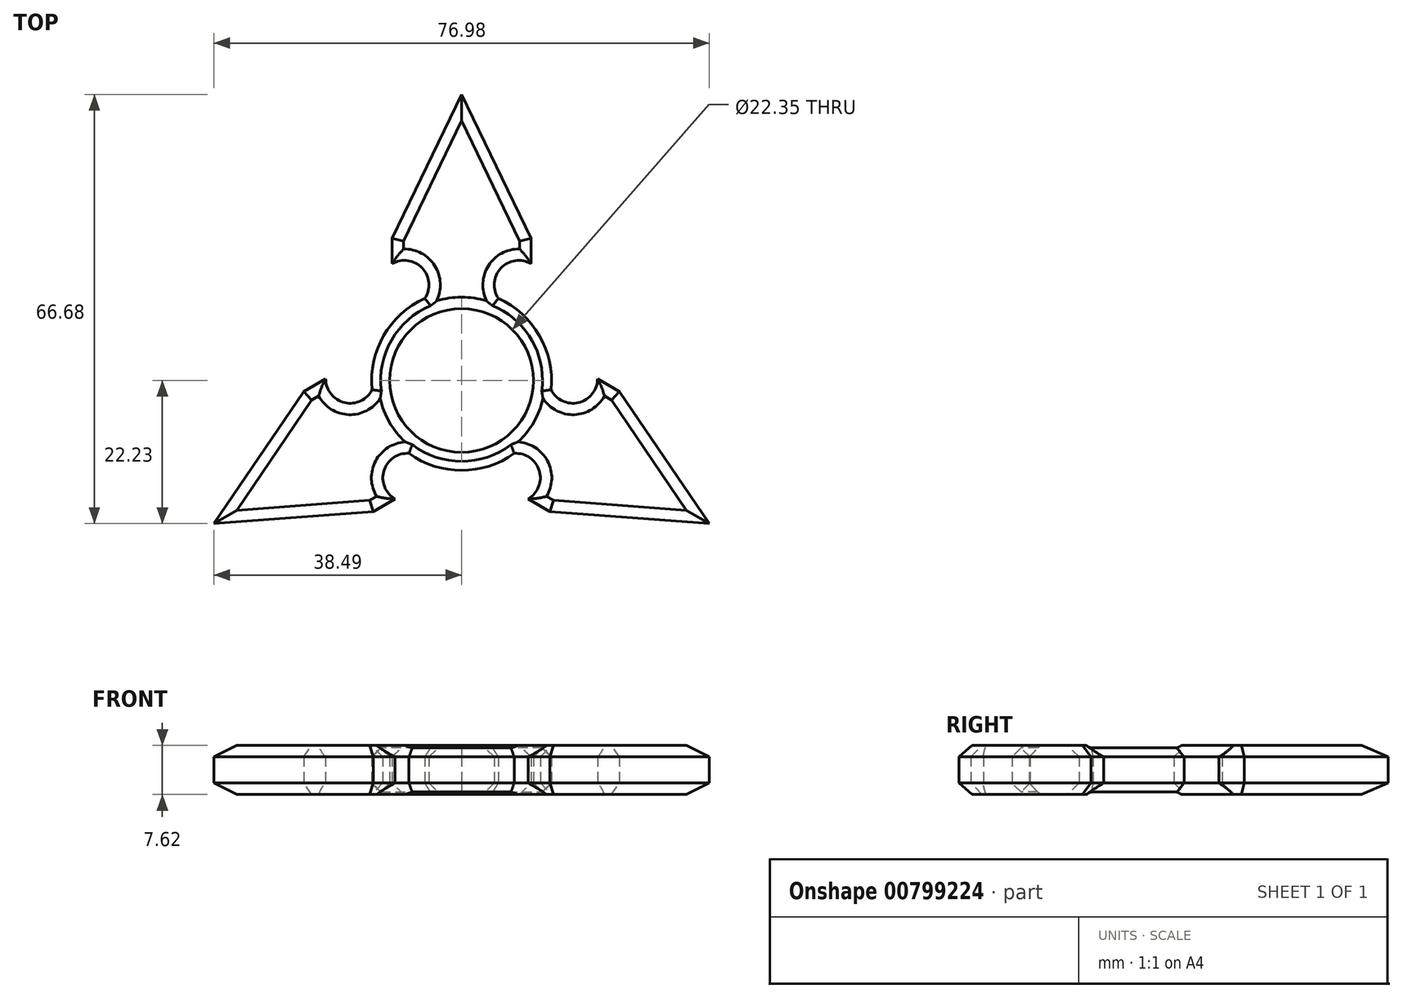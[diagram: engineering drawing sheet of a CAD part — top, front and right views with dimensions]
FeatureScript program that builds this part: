
annotation { "Feature Type Name" : "Feature", "Feature Type Description" : "" }
export const myFeature = defineFeature(function(context is Context, id is Id, definition is map)
    precondition{}
    {
        {
            var Q0;
            Q0=qCreatedBy(makeId("Top.planeOp"),FACE);
            var sketch = newSketch(context, id + "F0", { "sketchPlane" : qUnion([Q0])});
            skCircle(sketch, "E0", {"center": v(0, 0) * mm, "radius": 11.18 * mm});
            skCircle(sketch, "E1", {"center": v(0, 0) * mm, "radius": 13.97 * mm});
            skArc(sketch, "E2", {"start": v(-5.72, 12.75) * mm, "mid": v(-6.1, 17.46) * mm, "end": v(-10.78, 18.16) * mm});
            skLineSegment(sketch, "E3", {"start": v(-10.78, 18.16) * mm, "end": v(-10.78, 22.09) * mm});
            skLineSegment(sketch, "E4", {"start": v(-10.78, 22.09) * mm, "end": v(0, 44.45) * mm});
            skLineSegment(sketch, "E5.MirrorCS", {"start": v(10.78, 18.16) * mm, "end": v(10.78, 22.09) * mm});
            skArc(sketch, "E6.MirrorCS", {"start": v(5.72, 12.75) * mm, "mid": v(6.1, 17.46) * mm, "end": v(10.78, 18.16) * mm});
            skLineSegment(sketch, "E7.MirrorCS", {"start": v(10.78, 22.09) * mm, "end": v(0, 44.45) * mm});
            skLineSegment(sketch, "E8.1.0", {"start": v(-13.74, -20.38) * mm, "end": v(-38.5, -22.22) * mm});
            skLineSegment(sketch, "E8.1.1", {"start": v(-24.52, -1.7) * mm, "end": v(-38.5, -22.22) * mm});
            skArc(sketch, "E8.1.2", {"start": v(-13.9, -1.42) * mm, "mid": v(-18.17, -3.44) * mm, "end": v(-21.12, 0.25) * mm});
            skArc(sketch, "E8.1.3", {"start": v(-8.18, -11.32) * mm, "mid": v(-12.06, -14.02) * mm, "end": v(-10.34, -18.42) * mm});
            skLineSegment(sketch, "E8.1.4", {"start": v(-10.34, -18.42) * mm, "end": v(-13.74, -20.38) * mm});
            skLineSegment(sketch, "E8.1.5", {"start": v(-21.12, 0.25) * mm, "end": v(-24.52, -1.7) * mm});
            skLineSegment(sketch, "E8.2.0", {"start": v(24.52, -1.7) * mm, "end": v(38.5, -22.23) * mm});
            skLineSegment(sketch, "E8.2.1", {"start": v(13.74, -20.38) * mm, "end": v(38.5, -22.22) * mm});
            skArc(sketch, "E8.2.2", {"start": v(8.18, -11.32) * mm, "mid": v(12.06, -14.02) * mm, "end": v(10.34, -18.42) * mm});
            skArc(sketch, "E8.2.3", {"start": v(13.9, -1.42) * mm, "mid": v(18.17, -3.44) * mm, "end": v(21.12, 0.25) * mm});
            skLineSegment(sketch, "E8.2.4", {"start": v(21.12, 0.25) * mm, "end": v(24.52, -1.7) * mm});
            skLineSegment(sketch, "E8.2.5", {"start": v(10.34, -18.42) * mm, "end": v(13.74, -20.38) * mm});
            skSolve(sketch);
        }
        {
            var Q0;
            {var subQ0=sQuery(id+"F0.wireOp",EDGE,"E2");Q0=makeQuery(id+"F0.imprint","IMPRINT",FACE,{"disambiguationData":[TD([[makeQuery(id+"F0.imprint","IMPRINT",EDGE,{"derivedFrom":subQ0}),-1.0]])]});}
            var Q1;
            Q1=makeQuery(id+"F0.imprint","IMPRINT",FACE,{"disambiguationData":[TD([[makeQuery(id+"F0.imprint","IMPRINT",EDGE,{"derivedFrom":sQuery(id+"F0.wireOp",EDGE,"E0")}),-1.0]])]});
            var Q2;
            Q2=makeQuery(id+"F0.imprint","IMPRINT",FACE,{"disambiguationData":[TD([[makeQuery(id+"F0.imprint","IMPRINT",EDGE,{"derivedFrom":sQuery(id+"F0.wireOp",EDGE,"E8.2.0")}),-1.0]])]});
            var Q3;
            Q3=makeQuery(id+"F0.imprint","IMPRINT",FACE,{"disambiguationData":[TD([[makeQuery(id+"F0.imprint","IMPRINT",EDGE,{"derivedFrom":sQuery(id+"F0.wireOp",EDGE,"E8.1.0")}),-1.0]])]});
            extrude(context, id + "F1", {"entities" : qUnion([Q0, Q1, Q2, Q3]), "depth" : 7.62 * mm, "offsetDistance" : 25.4 * mm});
        }
        {
            var Q0;
            Q0=makeQuery(id+"F1.opExtrude","CAP_FACE",FACE,{"disambiguationData":[OSD([sQuery(id+"F0.wireOp",EDGE,"E0"),sQuery(id+"F0.wireOp",EDGE,"E1"),sQuery(id+"F0.wireOp",EDGE,"E2"),sQuery(id+"F0.wireOp",EDGE,"E3"),sQuery(id+"F0.wireOp",EDGE,"E4"),sQuery(id+"F0.wireOp",EDGE,"E5.MirrorCS"),sQuery(id+"F0.wireOp",EDGE,"E6.MirrorCS"),sQuery(id+"F0.wireOp",EDGE,"E7.MirrorCS"),sQuery(id+"F0.wireOp",EDGE,"E8.1.0"),sQuery(id+"F0.wireOp",EDGE,"E8.1.1"),sQuery(id+"F0.wireOp",EDGE,"E8.1.2"),sQuery(id+"F0.wireOp",EDGE,"E8.1.3"),sQuery(id+"F0.wireOp",EDGE,"E8.1.4"),sQuery(id+"F0.wireOp",EDGE,"E8.1.5"),sQuery(id+"F0.wireOp",EDGE,"E8.2.0"),sQuery(id+"F0.wireOp",EDGE,"E8.2.1"),sQuery(id+"F0.wireOp",EDGE,"E8.2.2"),sQuery(id+"F0.wireOp",EDGE,"E8.2.3"),sQuery(id+"F0.wireOp",EDGE,"E8.2.4"),sQuery(id+"F0.wireOp",EDGE,"E8.2.5")])],"isStart":false});
            var Q1;
            Q1=makeQuery(id+"F1.opExtrude","CAP_FACE",FACE,{"disambiguationData":[OSD([sQuery(id+"F0.wireOp",EDGE,"E0"),sQuery(id+"F0.wireOp",EDGE,"E1"),sQuery(id+"F0.wireOp",EDGE,"E2"),sQuery(id+"F0.wireOp",EDGE,"E3"),sQuery(id+"F0.wireOp",EDGE,"E4"),sQuery(id+"F0.wireOp",EDGE,"E5.MirrorCS"),sQuery(id+"F0.wireOp",EDGE,"E6.MirrorCS"),sQuery(id+"F0.wireOp",EDGE,"E7.MirrorCS"),sQuery(id+"F0.wireOp",EDGE,"E8.1.0"),sQuery(id+"F0.wireOp",EDGE,"E8.1.1"),sQuery(id+"F0.wireOp",EDGE,"E8.1.2"),sQuery(id+"F0.wireOp",EDGE,"E8.1.3"),sQuery(id+"F0.wireOp",EDGE,"E8.1.4"),sQuery(id+"F0.wireOp",EDGE,"E8.1.5"),sQuery(id+"F0.wireOp",EDGE,"E8.2.0"),sQuery(id+"F0.wireOp",EDGE,"E8.2.1"),sQuery(id+"F0.wireOp",EDGE,"E8.2.2"),sQuery(id+"F0.wireOp",EDGE,"E8.2.3"),sQuery(id+"F0.wireOp",EDGE,"E8.2.4"),sQuery(id+"F0.wireOp",EDGE,"E8.2.5")])],"isStart":true});
            chamfer(context, id + "F2", {"entities" : qUnion([Q0, Q1]), "width" : 1.78 * mm, "tangentPropagation" : true});
        }
    });
